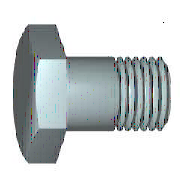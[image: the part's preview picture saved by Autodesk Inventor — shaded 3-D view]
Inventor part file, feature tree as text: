
AUTODESK INVENTOR PART (.ipt)
format: ipt  version: 2014 SP1 (Build 180222100, 222)  size: 190,464 bytes
history: native  units: mm (DEFAULTED — no unit token found)
features: sketch x2, extrude x1, chamfer x1, fillet x1, plane x1
ambient origin geometry x7: Origin, YZ Plane, XZ Plane, X Axis, Y Axis, Z Axis, Center Point
bodies: Solid1 (feature_tree), Body (feature_tree)
feature tree (6):
  extrude  "Head"  TaperAngle=90.0deg  [1 undecoded]
  chamfer  "Chamfer1"  [1 undecoded]
  fillet  "Fillet2"  [1 undecoded]
  plane  "Work Plane1"
  sketch  "Sketch1"  dims[d2=6.0mm d12=90.0deg]
  sketch  "Sketch2"  dims[d3=4.0mm d4=0.0mm d21=90.0deg d6=0.61345mm d7=0.61355mm d8=0.0mm d11=10.0mm d15=11.0mm d16=0.0mm d55=45.0deg d58=0.0mm d59=12.0mm d65=10.0mm d67=30.0deg d68=12.0mm d69=4.0mm d71=0.25mm d73=0.0mm]
note: 3 required parameter values undecoded (feature->parameter linkage not recoverable at this tier; creation-order binding heuristic only, values carry confidence <= 0.55)
